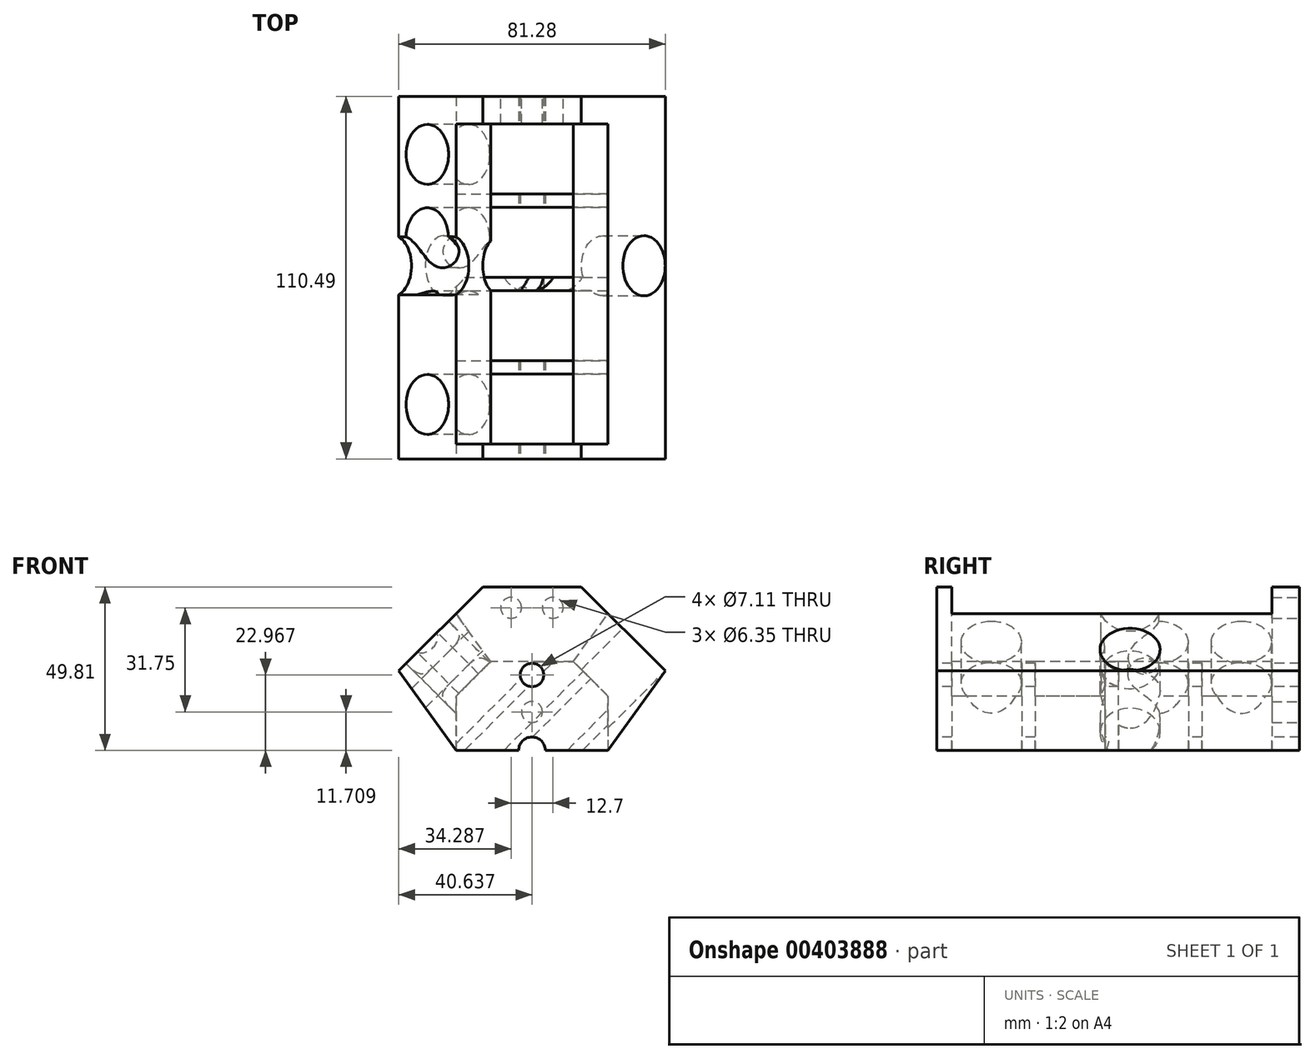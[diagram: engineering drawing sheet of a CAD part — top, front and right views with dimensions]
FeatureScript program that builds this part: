
annotation { "Feature Type Name" : "Feature", "Feature Type Description" : "" }
export const myFeature = defineFeature(function(context is Context, id is Id, definition is map)
    precondition{}
    {
        {
            var Q0;
            Q0=qCreatedBy(makeId("Top.planeOp"),FACE);
            var sketch = newSketch(context, id + "F0", { "sketchPlane" : qUnion([Q0])});
            skLineSegment(sketch, "E0.bottom", {"start": v(-50.32, 362.69) * mm, "end": v(356.08, 362.69) * mm});
            skLineSegment(sketch, "E0.top", {"start": v(-50.32, -189.76) * mm, "end": v(356.08, -189.76) * mm});
            skLineSegment(sketch, "E0.left", {"start": v(-50.32, 362.69) * mm, "end": v(-50.32, -189.76) * mm});
            skLineSegment(sketch, "E0.right", {"start": v(356.08, 362.69) * mm, "end": v(356.08, -189.76) * mm});
            skPoint(sketch, "E1.right.end.orphan", {"position": v(268.7, 221.15) * mm});
            skPoint(sketch, "E2.end.orphan", {"position": v(268.7, 119.55) * mm});
            skPoint(sketch, "E3.right.end.orphan", {"position": v(268.7, 66.78) * mm});
            skPoint(sketch, "E4.end.orphan", {"position": v(268.7, -34.82) * mm});
            skPoint(sketch, "E5.top.end.orphan", {"position": v(268.7, -62.76) * mm});
            skLineSegment(sketch, "E6.bottom", {"start": v(37.06, -166.9) * mm, "end": v(268.7, -166.9) * mm});
            skLineSegment(sketch, "E6.top", {"start": v(37.06, -60.22) * mm, "end": v(268.7, -60.22) * mm});
            skLineSegment(sketch, "E6.left", {"start": v(37.06, -166.9) * mm, "end": v(37.06, -60.22) * mm});
            skLineSegment(sketch, "E6.right", {"start": v(268.7, -166.9) * mm, "end": v(268.7, -60.22) * mm});
            skPoint(sketch, "E7.endSnap0", {"position": v(152.88, -189.76) * mm});
            skLineSegment(sketch, "E8.bottom", {"start": v(37.06, 320.78) * mm, "end": v(268.7, 320.78) * mm});
            skLineSegment(sketch, "E8.top", {"start": v(37.06, 214.1) * mm, "end": v(268.7, 214.1) * mm});
            skLineSegment(sketch, "E8.left", {"start": v(37.06, 320.78) * mm, "end": v(37.06, 214.1) * mm});
            skLineSegment(sketch, "E8.right", {"start": v(268.7, 320.78) * mm, "end": v(268.7, 214.1) * mm});
            skLineSegment(sketch, "E9.bottom", {"start": v(37.06, 193.78) * mm, "end": v(268.7, 193.78) * mm});
            skLineSegment(sketch, "E9.top", {"start": v(37.06, 87.1) * mm, "end": v(268.7, 87.1) * mm});
            skLineSegment(sketch, "E9.left", {"start": v(37.06, 193.78) * mm, "end": v(37.06, 87.1) * mm});
            skLineSegment(sketch, "E9.right", {"start": v(268.7, 193.78) * mm, "end": v(268.7, 87.1) * mm});
            skLineSegment(sketch, "E10.right", {"start": v(268.7, -34.82) * mm, "end": v(268.7, -39.9) * mm});
            skLineSegment(sketch, "E11.bottom", {"start": v(37.06, 66.78) * mm, "end": v(268.7, 66.78) * mm});
            skLineSegment(sketch, "E11.top", {"start": v(37.06, -39.9) * mm, "end": v(268.7, -39.9) * mm});
            skLineSegment(sketch, "E11.left", {"start": v(37.06, 66.78) * mm, "end": v(37.06, -39.9) * mm});
            skLineSegment(sketch, "E11.right", {"start": v(268.7, 66.78) * mm, "end": v(268.7, -39.9) * mm});
            skPoint(sketch, "E7.end.orphan", {"position": v(268.7, -189.76) * mm});
            skPoint(sketch, "E12.start.orphan", {"position": v(268.7, 320.78) * mm});
            skSolve(sketch);
        }
        {
            var Q0;
            Q0=makeQuery(id+"F0.imprint","IMPRINT",FACE,{"disambiguationData":[TD([[makeQuery(id+"F0.imprint","IMPRINT",EDGE,{"derivedFrom":sQuery(id+"F0.wireOp",EDGE,"E0.bottom")}),-1.0]])]});
            extrude(context, id + "F1", {"entities" : qUnion([Q0]), "depth" : 249.05 * mm});
        }
        {
            var Q0;
            Q0=makeQuery(id+"F1.opExtrude","SWEPT_FACE",FACE,{"disambiguationData":[OSD([sQuery(id+"F0.wireOp",EDGE,"E0.top")])]});
            var sketch = newSketch(context, id + "F2", { "sketchPlane" : qUnion([Q0])});
            skLineSegment(sketch, "E13", {"start": v(152.88, 0) * mm, "end": v(37.06, 0) * mm, "construction": true});
            skLineSegment(sketch, "E14", {"start": v(152.88, 0) * mm, "end": v(268.7, 0) * mm, "construction": true});
            skLineSegment(sketch, "E15", {"start": v(152.88, 0) * mm, "end": v(152.88, -265.94) * mm, "construction": true});
            skLineSegment(sketch, "E16", {"start": v(152.88, 0) * mm, "end": v(-102.56, -255.45) * mm, "construction": true});
            skLineSegment(sketch, "E17", {"start": v(-22.58, -175.46) * mm, "end": v(-184.67, -13.37) * mm, "construction": true});
            skLineSegment(sketch, "E18", {"start": v(-184.67, -13.37) * mm, "end": v(-50.32, 120.99) * mm, "construction": true});
            skLineSegment(sketch, "E19", {"start": v(37.06, 0) * mm, "end": v(-50.32, 120.99) * mm});
            skLineSegment(sketch, "E20", {"start": v(-50.32, 0) * mm, "end": v(37.06, 0) * mm});
            skLineSegment(sketch, "E21", {"start": v(-50.32, 120.99) * mm, "end": v(-50.32, 0) * mm});
            skLineSegment(sketch, "E22", {"start": v(152.88, 0) * mm, "end": v(426.24, -273.36) * mm, "construction": true});
            skLineSegment(sketch, "E23", {"start": v(328.35, -175.46) * mm, "end": v(490.44, -13.37) * mm, "construction": true});
            skLineSegment(sketch, "E24", {"start": v(490.44, -13.37) * mm, "end": v(356.08, 120.99) * mm, "construction": true});
            skLineSegment(sketch, "E25", {"start": v(268.7, 0) * mm, "end": v(356.08, 120.99) * mm});
            skLineSegment(sketch, "E26", {"start": v(356.08, 120.99) * mm, "end": v(356.08, 0) * mm});
            skLineSegment(sketch, "E27", {"start": v(268.7, 0) * mm, "end": v(356.08, 0) * mm});
            skLineSegment(sketch, "E28", {"start": v(-184.67, -13.37) * mm, "end": v(77.74, 249.05) * mm, "construction": true});
            skLineSegment(sketch, "E29", {"start": v(490.44, -13.37) * mm, "end": v(228.02, 249.05) * mm, "construction": true});
            skLineSegment(sketch, "E30", {"start": v(77.74, 249.05) * mm, "end": v(-50.32, 249.05) * mm});
            skLineSegment(sketch, "E31", {"start": v(-50.32, 249.05) * mm, "end": v(-50.32, 120.99) * mm});
            skLineSegment(sketch, "E32", {"start": v(-50.32, 120.99) * mm, "end": v(77.74, 249.05) * mm});
            skLineSegment(sketch, "E33", {"start": v(228.02, 249.05) * mm, "end": v(356.08, 249.05) * mm});
            skLineSegment(sketch, "E34", {"start": v(356.08, 249.05) * mm, "end": v(356.08, 120.99) * mm});
            skLineSegment(sketch, "E35", {"start": v(356.08, 120.99) * mm, "end": v(228.02, 249.05) * mm});
            skLineSegment(sketch, "E36", {"start": v(152.88, 249.05) * mm, "end": v(152.88, 344.64) * mm, "construction": true});
            skLineSegment(sketch, "E37", {"start": v(152.88, 344.64) * mm, "end": v(46.2, 344.64) * mm, "construction": true});
            skLineSegment(sketch, "E38", {"start": v(152.88, 344.64) * mm, "end": v(259.56, 344.64) * mm, "construction": true});
            skLineSegment(sketch, "E39", {"start": v(259.56, 344.64) * mm, "end": v(259.56, 217.5) * mm, "construction": true});
            skLineSegment(sketch, "E40", {"start": v(46.2, 344.64) * mm, "end": v(46.2, 217.5) * mm, "construction": true});
            skCircle(sketch, "E41", {"center": v(152.88, 0) * mm, "radius": 20.32 * mm});
            skLineSegment(sketch, "E42", {"start": v(152.88, 0) * mm, "end": v(152.88, 114.83) * mm, "construction": true});
            skCircle(sketch, "E43", {"center": v(152.88, 114.83) * mm, "radius": 17.78 * mm});
            skLineSegment(sketch, "E44", {"start": v(152.88, 114.83) * mm, "end": v(152.88, 132.61) * mm, "construction": true});
            skLineSegment(sketch, "E45", {"start": v(152.88, 132.61) * mm, "end": v(152.88, 249.05) * mm, "construction": true});
            skLineSegment(sketch, "E46", {"start": v(152.88, 249.05) * mm, "end": v(152.88, 147.45) * mm});
            skSolve(sketch);
        }
        {
            var Q0;
            Q0=makeQuery(id+"F2.imprint","IMPRINT",FACE,{"disambiguationData":[TD([[makeQuery(id+"F2.imprint","IMPRINT",EDGE,{"derivedFrom":sQuery(id+"F2.wireOp",EDGE,"E19")}),1.0]])]});
            extrude(context, id + "F3", {"entities" : qUnion([Q0]), "operationType" : NewBodyOperationType.REMOVE, "oppositeDirection" : true, "depth" : 1497.04 * mm});
        }
        {
            var Q0;
            Q0=makeQuery(id+"F2.imprint","IMPRINT",FACE,{"disambiguationData":[TD([[makeQuery(id+"F2.imprint","IMPRINT",EDGE,{"derivedFrom":sQuery(id+"F2.wireOp",EDGE,"E25")}),-1.0]])]});
            extrude(context, id + "F4", {"entities" : qUnion([Q0]), "operationType" : NewBodyOperationType.REMOVE, "oppositeDirection" : true, "depth" : 679.38 * mm});
        }
        {
            var Q0;
            Q0=makeQuery(id+"F2.imprint","IMPRINT",FACE,{"disambiguationData":[TD([[makeQuery(id+"F2.imprint","IMPRINT",EDGE,{"derivedFrom":sQuery(id+"F2.wireOp",EDGE,"E30")}),-1.0]])]});
            extrude(context, id + "F5", {"entities" : qUnion([Q0]), "operationType" : NewBodyOperationType.REMOVE, "oppositeDirection" : true, "depth" : 711.26 * mm});
        }
        {
            var Q0;
            Q0=makeQuery(id+"F2.imprint","IMPRINT",FACE,{"disambiguationData":[TD([[makeQuery(id+"F2.imprint","IMPRINT",EDGE,{"derivedFrom":sQuery(id+"F2.wireOp",EDGE,"E33")}),-1.0]])]});
            extrude(context, id + "F6", {"entities" : qUnion([Q0]), "operationType" : NewBodyOperationType.REMOVE, "oppositeDirection" : true, "depth" : 1229.88 * mm});
        }
        {
            var Q0;
            {var subQ0=sQuery(id+"F2.wireOp",EDGE,"E41");var subQ1=makeQuery(id+"F1.opExtrude","CAP_EDGE",EDGE,{"disambiguationData":[OSD([sQuery(id+"F0.wireOp",EDGE,"E0.top")])],"isStart":true});var subQ2=makeQuery(id+"F2.imprint","INTERSECT",VERTEX,{"disambiguationData":[OD(0.0)],"derivedFrom":[subQ1,subQ0]});Q0=makeQuery(id+"F2.imprint","IMPRINT",FACE,{"disambiguationData":[TD([[makeQuery(id+"F2.imprint","IMPRINT",EDGE,{"disambiguationData":[TD([[subQ2,1.0]])],"derivedFrom":subQ0}),1.0]])]});}
            extrude(context, id + "F7", {"entities" : qUnion([Q0]), "operationType" : NewBodyOperationType.REMOVE, "oppositeDirection" : true, "depth" : 578.05 * mm});
        }
        {
            var Q0;
            Q0=makeQuery(id+"F2.imprint","IMPRINT",FACE,{"disambiguationData":[TD([[makeQuery(id+"F2.imprint","IMPRINT",EDGE,{"derivedFrom":sQuery(id+"F2.wireOp",EDGE,"E43")}),1.0]])]});
            extrude(context, id + "F8", {"entities" : qUnion([Q0]), "operationType" : NewBodyOperationType.REMOVE, "oppositeDirection" : true, "depth" : 729.74 * mm});
        }
        {
            var Q0;
            Q0=makeQuery(id+"F1.opExtrude","SWEPT_FACE",FACE,{"disambiguationData":[OSD([sQuery(id+"F0.wireOp",EDGE,"E6.top")])]});
            var sketch = newSketch(context, id + "F9", { "sketchPlane" : qUnion([Q0])});
            skPoint(sketch, "E47.endSnap0", {"position": v(152.88, 249.05) * mm});
            skLineSegment(sketch, "E48", {"start": v(152.88, 135.38) * mm, "end": v(37.06, 135.38) * mm});
            skLineSegment(sketch, "E49", {"start": v(37.06, 135.38) * mm, "end": v(268.7, 135.38) * mm});
            skLineSegment(sketch, "E50", {"start": v(268.7, 135.38) * mm, "end": v(268.7, 208.36) * mm});
            skLineSegment(sketch, "E51", {"start": v(268.7, 208.36) * mm, "end": v(228.02, 249.05) * mm});
            skLineSegment(sketch, "E52", {"start": v(228.02, 249.05) * mm, "end": v(77.74, 249.05) * mm});
            skLineSegment(sketch, "E53", {"start": v(77.74, 249.05) * mm, "end": v(37.06, 208.36) * mm});
            skLineSegment(sketch, "E54", {"start": v(37.06, 135.38) * mm, "end": v(37.06, 208.36) * mm});
            skLineSegment(sketch, "E55", {"start": v(37.06, 208.36) * mm, "end": v(89.77, 135.38) * mm});
            skLineSegment(sketch, "E56", {"start": v(268.7, 208.36) * mm, "end": v(216, 135.38) * mm});
            skSolve(sketch);
        }
        {
            var Q0;
            Q0=makeQuery(id+"F9.imprint","IMPRINT",FACE,{"disambiguationData":[TD([[makeQuery(id+"F9.imprint","IMPRINT",EDGE,{"derivedFrom":sQuery(id+"F9.wireOp",EDGE,"E51")}),-1.0]])]});
            extrude(context, id + "F10", {"entities" : qUnion([Q0]), "operationType" : NewBodyOperationType.REMOVE, "oppositeDirection" : true, "depth" : 324.26 * mm});
        }
        {
            var Q0;
            Q0=makeQuery(id+"F1.opExtrude","SWEPT_FACE",FACE,{"disambiguationData":[OSD([sQuery(id+"F0.wireOp",EDGE,"E11.top")])]});
            var sketch = newSketch(context, id + "F11", { "sketchPlane" : qUnion([Q0])});
            skLineSegment(sketch, "E57", {"start": v(-89.77, 135.38) * mm, "end": v(-37.06, 208.36) * mm});
            skLineSegment(sketch, "E58", {"start": v(-89.77, 135.38) * mm, "end": v(-37.06, 135.38) * mm});
            skLineSegment(sketch, "E59", {"start": v(-37.06, 135.38) * mm, "end": v(-37.06, 208.36) * mm});
            skSolve(sketch);
        }
        {
            var Q0;
            Q0=qSketchRegion(id+"F11",true);
            extrude(context, id + "F12", {"entities" : qUnion([Q0]), "operationType" : NewBodyOperationType.ADD, "depth" : 368.3 * mm, "hasSecondDirection" : true, "secondDirectionOppositeDirection" : true, "secondDirectionDepth" : 127 * mm});
        }
        {
            var Q0;
            Q0=makeQuery(id+"F1.opExtrude","SWEPT_FACE",FACE,{"disambiguationData":[OSD([sQuery(id+"F0.wireOp",EDGE,"E11.top")])]});
            var sketch = newSketch(context, id + "F13", { "sketchPlane" : qUnion([Q0])});
            skLineSegment(sketch, "E60", {"start": v(-216, 135.38) * mm, "end": v(-268.7, 135.38) * mm});
            skLineSegment(sketch, "E61", {"start": v(-268.7, 135.38) * mm, "end": v(-268.7, 208.36) * mm});
            skLineSegment(sketch, "E62", {"start": v(-268.7, 208.36) * mm, "end": v(-216, 135.38) * mm});
            skSolve(sketch);
        }
        {
            var Q0;
            Q0=qSketchRegion(id+"F13",true);
            extrude(context, id + "F14", {"entities" : qUnion([Q0]), "operationType" : NewBodyOperationType.ADD, "depth" : 368.3 * mm, "hasSecondDirection" : true, "secondDirectionOppositeDirection" : true, "secondDirectionDepth" : 127 * mm});
        }
        {
            var Q0;
            Q0=makeQuery(id+"F1.opExtrude","SWEPT_FACE",FACE,{"disambiguationData":[OSD([sQuery(id+"F0.wireOp",EDGE,"E9.top")])]});
            var sketch = newSketch(context, id + "F15", { "sketchPlane" : qUnion([Q0])});
            skLineSegment(sketch, "E63", {"start": v(-89.77, 135.38) * mm, "end": v(-37.06, 82.68) * mm});
            skLineSegment(sketch, "E64", {"start": v(-37.06, 82.68) * mm, "end": v(-37.06, 135.38) * mm});
            skLineSegment(sketch, "E65", {"start": v(-37.06, 135.38) * mm, "end": v(-89.77, 135.38) * mm});
            skLineSegment(sketch, "E66", {"start": v(-216, 135.38) * mm, "end": v(-268.7, 82.68) * mm});
            skLineSegment(sketch, "E67", {"start": v(-268.7, 82.68) * mm, "end": v(-268.7, 135.38) * mm});
            skLineSegment(sketch, "E68", {"start": v(-268.7, 135.38) * mm, "end": v(-216, 135.38) * mm});
            skSolve(sketch);
        }
        {
            var Q0;
            Q0=makeQuery(id+"F15.imprint","IMPRINT",FACE,{"disambiguationData":[TD([[makeQuery(id+"F15.imprint","IMPRINT",EDGE,{"derivedFrom":sQuery(id+"F15.wireOp",EDGE,"E63")}),1.0]])]});
            extrude(context, id + "F16", {"entities" : qUnion([Q0]), "operationType" : NewBodyOperationType.ADD, "depth" : 249.12 * mm, "hasSecondDirection" : true, "secondDirectionOppositeDirection" : true, "secondDirectionDepth" : 267.4 * mm});
        }
        {
            var Q0;
            Q0=makeQuery(id+"F15.imprint","IMPRINT",FACE,{"disambiguationData":[TD([[makeQuery(id+"F15.imprint","IMPRINT",EDGE,{"derivedFrom":sQuery(id+"F15.wireOp",EDGE,"E66")}),-1.0]])]});
            extrude(context, id + "F17", {"entities" : qUnion([Q0]), "operationType" : NewBodyOperationType.ADD, "depth" : 272.47 * mm, "hasSecondDirection" : true, "secondDirectionOppositeDirection" : true, "secondDirectionDepth" : 265.33 * mm});
        }
        {
            var Q0;
            Q0=makeQuery(id+"F6.boolean.opBoolean","COPY",FACE,{"derivedFrom":makeQuery(id+"F6.opExtrude","SWEPT_FACE",FACE,{"disambiguationData":[OSD([sQuery(id+"F2.wireOp",EDGE,"E35")])]})});
            var sketch = newSketch(context, id + "F18", { "sketchPlane" : qUnion([Q0])});
            skLineSegment(sketch, "E69", {"start": v(42.67, -166.9) * mm, "end": v(166.24, -166.9) * mm});
            skLineSegment(sketch, "E70", {"start": v(42.67, 320.78) * mm, "end": v(166.24, 320.78) * mm});
            skLineSegment(sketch, "E71", {"start": v(104.45, -166.9) * mm, "end": v(104.45, -60.22) * mm});
            skLineSegment(sketch, "E72", {"start": v(104.45, -39.9) * mm, "end": v(104.45, 66.78) * mm});
            skLineSegment(sketch, "E73", {"start": v(104.45, 87.1) * mm, "end": v(104.45, 193.78) * mm});
            skLineSegment(sketch, "E74", {"start": v(104.45, 214.1) * mm, "end": v(104.45, 320.78) * mm});
            skLineSegment(sketch, "E75", {"start": v(104.45, -113.56) * mm, "end": v(166.24, -113.56) * mm});
            skLineSegment(sketch, "E76", {"start": v(104.45, 13.44) * mm, "end": v(166.24, 13.44) * mm});
            skLineSegment(sketch, "E77", {"start": v(104.45, 140.44) * mm, "end": v(166.24, 140.44) * mm});
            skLineSegment(sketch, "E78", {"start": v(104.45, 267.44) * mm, "end": v(166.24, 267.44) * mm});
            skLineSegment(sketch, "E79", {"start": v(119.9, -120.23) * mm, "end": v(104.45, -120.23) * mm});
            skCircle(sketch, "E80", {"center": v(104.45, -120.23) * mm, "radius": 45.72 * mm});
            skLineSegment(sketch, "E81", {"start": v(135.35, 13.44) * mm, "end": v(135.35, 6.75) * mm});
            skLineSegment(sketch, "E82", {"start": v(135.35, 140.44) * mm, "end": v(135.35, 133.75) * mm});
            skLineSegment(sketch, "E83", {"start": v(135.35, 267.44) * mm, "end": v(135.35, 260.75) * mm});
            skLineSegment(sketch, "E84", {"start": v(135.35, 6.75) * mm, "end": v(104.45, 6.75) * mm});
            skLineSegment(sketch, "E85", {"start": v(135.35, 133.75) * mm, "end": v(104.45, 133.75) * mm});
            skLineSegment(sketch, "E86", {"start": v(135.35, 260.75) * mm, "end": v(104.45, 260.75) * mm});
            skCircle(sketch, "E87", {"center": v(104.45, 6.75) * mm, "radius": 45.72 * mm});
            skCircle(sketch, "E88", {"center": v(104.45, 133.75) * mm, "radius": 45.72 * mm});
            skCircle(sketch, "E89", {"center": v(104.45, 260.75) * mm, "radius": 45.72 * mm});
            skSolve(sketch);
        }
        {
            var Q0;
            Q0=qSketchRegion(id+"F18",true);
            var Q1;
            {var subQ4=sQuery(id+"F18.wireOp",EDGE,"E81");Q1=makeQuery(id+"F18.imprint","IMPRINT",FACE,{"disambiguationData":[TD([[makeQuery(id+"F18.imprint","IMPRINT",EDGE,{"derivedFrom":subQ4}),-1.0]])]});}
            var Q2;
            {var subQ4=sQuery(id+"F18.wireOp",EDGE,"E82");Q2=makeQuery(id+"F18.imprint","IMPRINT",FACE,{"disambiguationData":[TD([[makeQuery(id+"F18.imprint","IMPRINT",EDGE,{"derivedFrom":subQ4}),-1.0]])]});}
            var Q3;
            {var subQ4=sQuery(id+"F18.wireOp",EDGE,"E83");Q3=makeQuery(id+"F18.imprint","IMPRINT",FACE,{"disambiguationData":[TD([[makeQuery(id+"F18.imprint","IMPRINT",EDGE,{"derivedFrom":subQ4}),-1.0]])]});}
            extrude(context, id + "F19", {"entities" : qUnion([Q0, Q1, Q2, Q3]), "operationType" : NewBodyOperationType.REMOVE, "oppositeDirection" : true, "depth" : 558.8 * mm});
        }
        {
            var Q0;
            Q0=makeQuery(id+"F5.boolean.opBoolean","COPY",FACE,{"derivedFrom":makeQuery(id+"F5.opExtrude","SWEPT_FACE",FACE,{"disambiguationData":[OSD([sQuery(id+"F2.wireOp",EDGE,"E32")])]})});
            var sketch = newSketch(context, id + "F20", { "sketchPlane" : qUnion([Q0])});
            skLineSegment(sketch, "E90", {"start": v(-320.78, 173.54) * mm, "end": v(-320.78, 49.97) * mm});
            skLineSegment(sketch, "E91", {"start": v(-320.78, 111.76) * mm, "end": v(-319.84, 111.76) * mm});
            skLineSegment(sketch, "E92", {"start": v(-193.78, 111.76) * mm, "end": v(-192.84, 111.76) * mm});
            skLineSegment(sketch, "E93", {"start": v(-66.78, 111.76) * mm, "end": v(-65.84, 111.76) * mm});
            skLineSegment(sketch, "E94", {"start": v(60.22, 111.76) * mm, "end": v(61.16, 111.76) * mm});
            skCircle(sketch, "E95", {"center": v(-274.12, 111.76) * mm, "radius": 45.72 * mm});
            skCircle(sketch, "E96", {"center": v(-147.12, 111.76) * mm, "radius": 45.72 * mm});
            skCircle(sketch, "E97", {"center": v(-20.12, 111.76) * mm, "radius": 45.72 * mm});
            skCircle(sketch, "E98", {"center": v(106.88, 111.76) * mm, "radius": 45.72 * mm});
            skPoint(sketch, "E99.start.orphan", {"position": v(-267.44, 111.76) * mm});
            skLineSegment(sketch, "E100.trimOffspring", {"start": v(-228.4, 111.76) * mm, "end": v(-214.1, 111.76) * mm});
            skLineSegment(sketch, "E101.trimOffspring", {"start": v(-101.4, 111.76) * mm, "end": v(-87.1, 111.76) * mm});
            skPoint(sketch, "E102.orphan", {"position": v(-140.44, 111.76) * mm});
            skPoint(sketch, "E103.start.orphan", {"position": v(-13.44, 111.76) * mm});
            skLineSegment(sketch, "E104.trimOffspring", {"start": v(25.6, 111.76) * mm, "end": v(39.9, 111.76) * mm});
            skPoint(sketch, "E105.start.orphan", {"position": v(113.56, 111.76) * mm});
            skLineSegment(sketch, "E106.trimOffspring", {"start": v(152.6, 111.76) * mm, "end": v(166.9, 111.76) * mm});
            skSolve(sketch);
        }
        {
            var Q0;
            {var subQ0=sQuery(id+"F20.wireOp",EDGE,"E95");var subQ1=makeQuery(id+"F20.imprint","IMPRINT",VERTEX,{"disambiguationData":[OD(0.0)],"derivedFrom":subQ0});Q0=makeQuery(id+"F20.imprint","IMPRINT",FACE,{"disambiguationData":[TD([[makeQuery(id+"F20.imprint","IMPRINT",EDGE,{"disambiguationData":[TD([[subQ1,1.0]])],"derivedFrom":subQ0}),1.0]])]});}
            var Q1;
            {var subQ0=sQuery(id+"F20.wireOp",EDGE,"E96");var subQ1=makeQuery(id+"F20.imprint","IMPRINT",VERTEX,{"disambiguationData":[OD(0.0)],"derivedFrom":subQ0});Q1=makeQuery(id+"F20.imprint","IMPRINT",FACE,{"disambiguationData":[TD([[makeQuery(id+"F20.imprint","IMPRINT",EDGE,{"disambiguationData":[TD([[subQ1,1.0]])],"derivedFrom":subQ0}),1.0]])]});}
            var Q2;
            {var subQ0=sQuery(id+"F20.wireOp",EDGE,"E97");var subQ1=makeQuery(id+"F20.imprint","IMPRINT",VERTEX,{"disambiguationData":[OD(0.0)],"derivedFrom":subQ0});Q2=makeQuery(id+"F20.imprint","IMPRINT",FACE,{"disambiguationData":[TD([[makeQuery(id+"F20.imprint","IMPRINT",EDGE,{"disambiguationData":[TD([[subQ1,1.0]])],"derivedFrom":subQ0}),1.0]])]});}
            var Q3;
            {var subQ0=sQuery(id+"F20.wireOp",EDGE,"E98");var subQ1=makeQuery(id+"F20.imprint","IMPRINT",VERTEX,{"disambiguationData":[OD(0.0)],"derivedFrom":subQ0});Q3=makeQuery(id+"F20.imprint","IMPRINT",FACE,{"disambiguationData":[TD([[makeQuery(id+"F20.imprint","IMPRINT",EDGE,{"disambiguationData":[TD([[subQ1,1.0]])],"derivedFrom":subQ0}),1.0]])]});}
            extrude(context, id + "F21", {"entities" : qUnion([Q0, Q1, Q2, Q3]), "operationType" : NewBodyOperationType.REMOVE, "oppositeDirection" : true, "depth" : 558.8 * mm});
        }
        {
            var Q0;
            Q0=makeQuery(id+"F1.opExtrude","SWEPT_BODY",BODY,{"disambiguationData":[OSD([sQuery(id+"F0.wireOp",EDGE,"E0.bottom"),sQuery(id+"F0.wireOp",EDGE,"E0.top"),sQuery(id+"F0.wireOp",EDGE,"E0.left"),sQuery(id+"F0.wireOp",EDGE,"E0.right"),sQuery(id+"F0.wireOp",EDGE,"E6.bottom"),sQuery(id+"F0.wireOp",EDGE,"E6.top"),sQuery(id+"F0.wireOp",EDGE,"E6.left"),sQuery(id+"F0.wireOp",EDGE,"E6.right"),sQuery(id+"F0.wireOp",EDGE,"E8.bottom"),sQuery(id+"F0.wireOp",EDGE,"E8.top"),sQuery(id+"F0.wireOp",EDGE,"E8.left"),sQuery(id+"F0.wireOp",EDGE,"E8.right"),sQuery(id+"F0.wireOp",EDGE,"E9.bottom"),sQuery(id+"F0.wireOp",EDGE,"E9.top"),sQuery(id+"F0.wireOp",EDGE,"E9.left"),sQuery(id+"F0.wireOp",EDGE,"E9.right"),sQuery(id+"F0.wireOp",EDGE,"E11.bottom"),sQuery(id+"F0.wireOp",EDGE,"E11.top"),sQuery(id+"F0.wireOp",EDGE,"E11.left"),sQuery(id+"F0.wireOp",EDGE,"E11.right")])]});
            var Q1;
            Q1=qCreatedBy(makeId("Origin.pointOp"),VERTEX);
            transform(context, id + "F22", {"entities" : qUnion([Q0]), "transformType" : TransformType.SCALE_UNIFORMLY, "scale" : .2, "scalePoint" : qUnion([Q1]), "makeCopy" : false});
        }
        {
            var Q0;
            Q0=makeQuery(id+"F1.opExtrude","SWEPT_FACE",FACE,{"disambiguationData":[OSD([sQuery(id+"F0.wireOp",EDGE,"E0.bottom")])]});
            var sketch = newSketch(context, id + "F23", { "sketchPlane" : qUnion([Q0])});
            skLineSegment(sketch, "E107", {"start": v(-30.58, 49.8) * mm, "end": v(-30.58, 37.1) * mm});
            skLineSegment(sketch, "E108", {"start": v(-30.58, 37.1) * mm, "end": v(-17.88, 37.1) * mm});
            skLineSegment(sketch, "E109", {"start": v(-30.58, 37.1) * mm, "end": v(-43.28, 37.1) * mm});
            skLineSegment(sketch, "E110", {"start": v(-43.28, 37.1) * mm, "end": v(-43.28, 49.8) * mm});
            skLineSegment(sketch, "E111", {"start": v(-17.88, 37.1) * mm, "end": v(-17.88, 49.8) * mm});
            skLineSegment(sketch, "E112", {"start": v(-43.28, 43.46) * mm, "end": v(-36.93, 43.46) * mm});
            skLineSegment(sketch, "E113", {"start": v(-17.88, 43.46) * mm, "end": v(-24.23, 43.46) * mm});
            skCircle(sketch, "E114", {"center": v(-36.93, 43.46) * mm, "radius": 3.18 * mm});
            skCircle(sketch, "E115", {"center": v(-24.23, 43.46) * mm, "radius": 3.18 * mm});
            skSolve(sketch);
        }
        {
            var Q0;
            Q0=qSketchRegion(id+"F23",true);
            extrude(context, id + "F24", {"entities" : qUnion([Q0]), "operationType" : NewBodyOperationType.REMOVE, "oppositeDirection" : true, "depth" : 25.4 * mm});
        }
        {
            var Q0;
            Q0=makeQuery(id+"F1.opExtrude","SWEPT_FACE",FACE,{"disambiguationData":[OSD([sQuery(id+"F0.wireOp",EDGE,"E0.bottom")])]});
            var sketch = newSketch(context, id + "F25", { "sketchPlane" : qUnion([Q0])});
            skLineSegment(sketch, "E116", {"start": v(-30.58, 49.8) * mm, "end": v(-30.58, 11.7) * mm});
            skCircle(sketch, "E117", {"center": v(-30.58, 11.7) * mm, "radius": 3.18 * mm});
            skSolve(sketch);
        }
        {
            var Q0;
            Q0=qSketchRegion(id+"F25",true);
            extrude(context, id + "F26", {"entities" : qUnion([Q0]), "operationType" : NewBodyOperationType.REMOVE, "oppositeDirection" : true, "depth" : 25.4 * mm});
        }
    });
